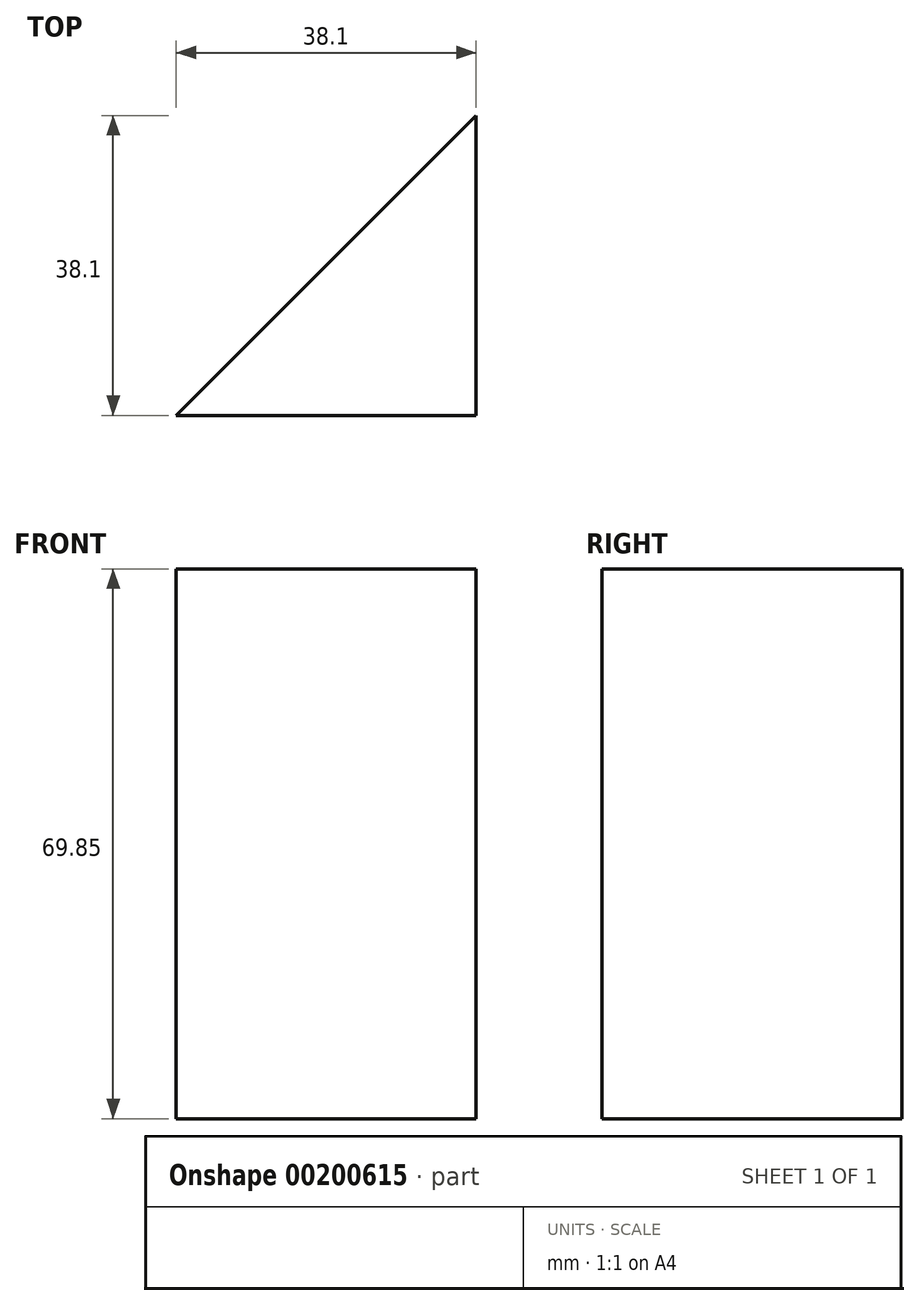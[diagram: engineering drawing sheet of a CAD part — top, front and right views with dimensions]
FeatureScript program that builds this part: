
annotation { "Feature Type Name" : "Feature", "Feature Type Description" : "" }
export const myFeature = defineFeature(function(context is Context, id is Id, definition is map)
    precondition{}
    {
        {
            var Q0;
            Q0=qCreatedBy(makeId("Top.planeOp"),FACE);
            var sketch = newSketch(context, id + "F0", { "sketchPlane" : qUnion([Q0])});
            skLineSegment(sketch, "E0", {"start": v(0, 0) * mm, "end": v(-38.1, 0) * mm});
            skLineSegment(sketch, "E1", {"start": v(-38.1, 0) * mm, "end": v(0, 38.1) * mm});
            skLineSegment(sketch, "E2", {"start": v(0, 38.1) * mm, "end": v(0, 0) * mm});
            skSolve(sketch);
        }
        {
            var Q0;
            Q0=makeQuery(id+"F0.imprint","IMPRINT",FACE,{"disambiguationData":[TD([[makeQuery(id+"F0.imprint","IMPRINT",EDGE,{"derivedFrom":sQuery(id+"F0.wireOp",EDGE,"E0")}),-1.0]])]});
            extrude(context, id + "F1", {"entities" : qUnion([Q0]), "depth" : 69.85 * mm});
        }
    });
